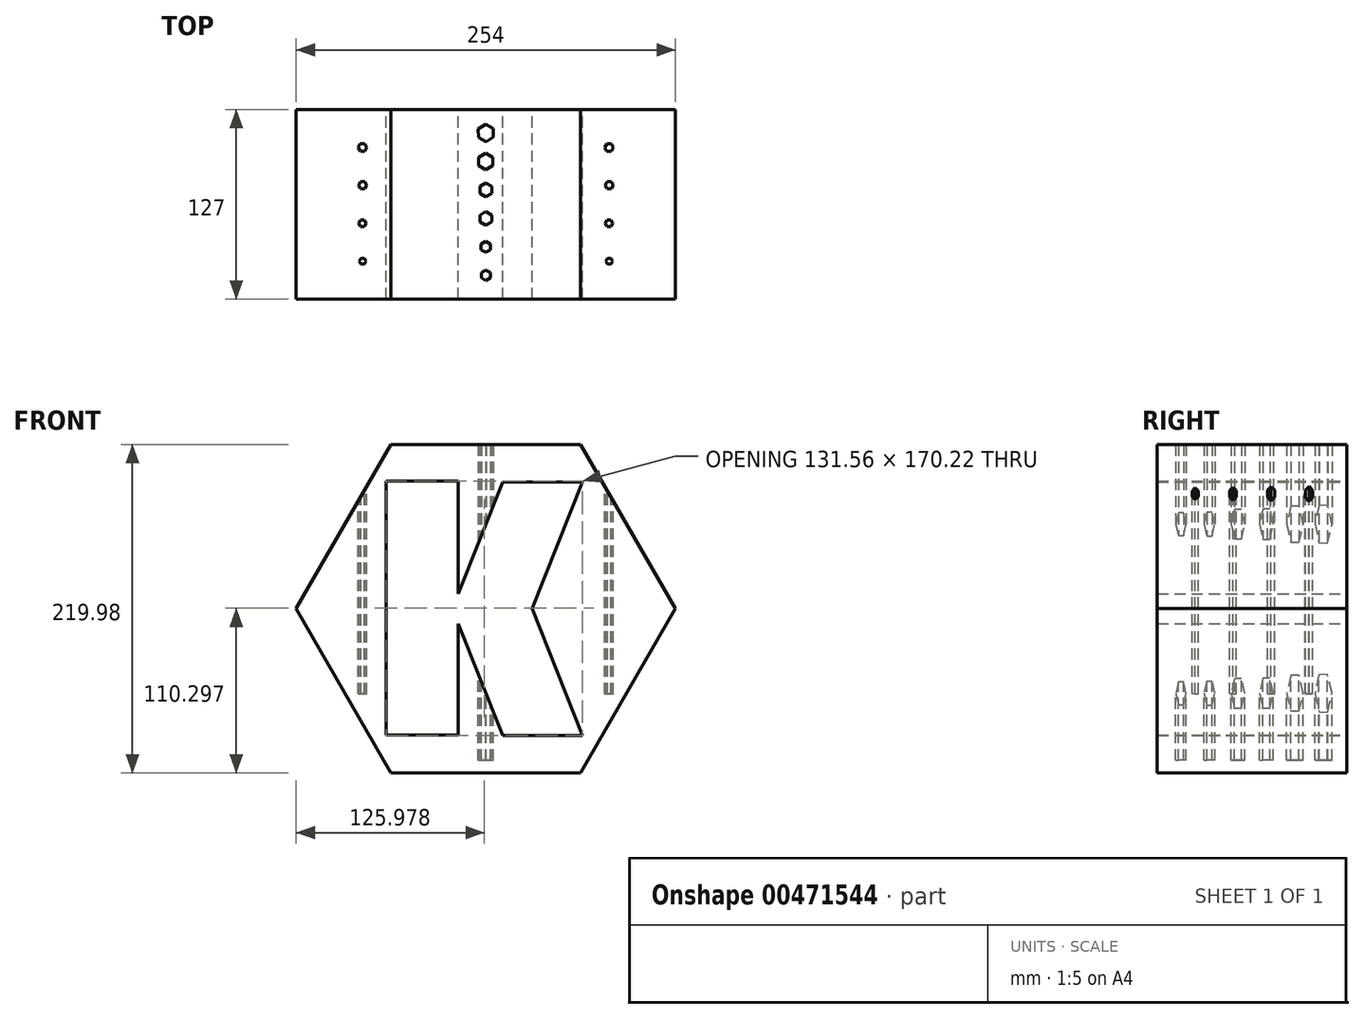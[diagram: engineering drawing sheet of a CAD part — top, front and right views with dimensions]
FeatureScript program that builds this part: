
annotation { "Feature Type Name" : "Feature", "Feature Type Description" : "" }
export const myFeature = defineFeature(function(context is Context, id is Id, definition is map)
    precondition{}
    {
        {
            var Q0;
            Q0=qCreatedBy(makeId("Front.planeOp"),FACE);
            var sketch = newSketch(context, id + "F0", { "sketchPlane" : qUnion([Q0])});
            skLineSegment(sketch, "E0.0", {"start": v(63.5, 109.99) * mm, "end": v(127, 0) * mm});
            skLineSegment(sketch, "E0.1", {"start": v(127, 0) * mm, "end": v(63.5, -109.99) * mm});
            skLineSegment(sketch, "E0.2", {"start": v(63.5, -109.99) * mm, "end": v(-63.5, -109.99) * mm});
            skLineSegment(sketch, "E0.3", {"start": v(-63.5, -109.99) * mm, "end": v(-127, 0) * mm});
            skLineSegment(sketch, "E0.4", {"start": v(-127, 0) * mm, "end": v(-63.5, 109.99) * mm});
            skLineSegment(sketch, "E0.5", {"start": v(-63.5, 109.99) * mm, "end": v(63.5, 109.99) * mm});
            skLineSegment(sketch, "E1.bottom", {"start": v(-66.8, 85.42) * mm, "end": v(-18.63, 85.42) * mm});
            skLineSegment(sketch, "E1.top", {"start": v(-66.8, -84.55) * mm, "end": v(-18.63, -84.55) * mm});
            skLineSegment(sketch, "E1.left", {"start": v(-66.8, 85.42) * mm, "end": v(-66.8, -84.55) * mm});
            skLineSegment(sketch, "E1.right", {"start": v(-18.63, 85.42) * mm, "end": v(-18.63, 9.98) * mm});
            skLineSegment(sketch, "E2.bottom", {"start": v(11.24, 84.8) * mm, "end": v(64.76, 84.8) * mm});
            skLineSegment(sketch, "E3.MirrorCS", {"start": v(11.24, -84.8) * mm, "end": v(64.76, -84.8) * mm});
            skLineSegment(sketch, "E4", {"start": v(11.24, 84.8) * mm, "end": v(-18.63, 9.98) * mm});
            skLineSegment(sketch, "E5.MirrorCS", {"start": v(11.24, -84.8) * mm, "end": v(-18.63, -9.98) * mm});
            skLineSegment(sketch, "E6", {"start": v(64.76, 84.8) * mm, "end": v(30.9, 0) * mm});
            skLineSegment(sketch, "E7.MirrorCS", {"start": v(64.76, -84.8) * mm, "end": v(30.9, 0) * mm});
            skLineSegment(sketch, "E8.trimOffspring", {"start": v(-18.63, -9.98) * mm, "end": v(-18.63, -84.55) * mm});
            skSolve(sketch);
        }
        {
            var Q0;
            Q0 = qSketchRegion(id + "F0", true);
            extrude(context, id + "F1", {"entities" : qUnion([Q0]), "endBound" : BoundingType.SYMMETRIC, "depth" : 127 * mm});
        }
        {
            var Q0;
            Q0=qCreatedBy(makeId("Top.planeOp"),FACE);
            var sketch = newSketch(context, id + "F2", { "sketchPlane" : qUnion([Q0])});
            skCircle(sketch, "E9.cCircle", {"center": v(-82.55, 38.1) * mm, "radius": 2.5 * mm, "construction": true});
            skLineSegment(sketch, "E9.0", {"start": v(-83.9, 35.55) * mm, "end": v(-85.44, 38) * mm});
            skLineSegment(sketch, "E9.1", {"start": v(-85.44, 38) * mm, "end": v(-84.08, 40.55) * mm});
            skLineSegment(sketch, "E9.2", {"start": v(-84.08, 40.55) * mm, "end": v(-81.2, 40.65) * mm});
            skLineSegment(sketch, "E9.3", {"start": v(-81.2, 40.65) * mm, "end": v(-79.66, 38.2) * mm});
            skLineSegment(sketch, "E9.4", {"start": v(-79.66, 38.2) * mm, "end": v(-81.02, 35.65) * mm});
            skLineSegment(sketch, "E9.5", {"start": v(-81.02, 35.65) * mm, "end": v(-83.9, 35.55) * mm});
            skPoint(sketch, "E9.0.midPoint", {"position": v(-84.67, 36.77) * mm});
            skCircle(sketch, "E10.cCircle", {"center": v(-82.55, 12.7) * mm, "radius": 2.38 * mm, "construction": true});
            skLineSegment(sketch, "E10.0", {"start": v(-83.92, 15.08) * mm, "end": v(-81.18, 15.08) * mm});
            skLineSegment(sketch, "E10.1", {"start": v(-81.18, 15.08) * mm, "end": v(-79.8, 12.7) * mm});
            skLineSegment(sketch, "E10.2", {"start": v(-79.8, 12.7) * mm, "end": v(-81.18, 10.32) * mm});
            skLineSegment(sketch, "E10.3", {"start": v(-81.18, 10.32) * mm, "end": v(-83.92, 10.32) * mm});
            skLineSegment(sketch, "E10.4", {"start": v(-83.92, 10.32) * mm, "end": v(-85.3, 12.7) * mm});
            skLineSegment(sketch, "E10.5", {"start": v(-85.3, 12.7) * mm, "end": v(-83.92, 15.08) * mm});
            skPoint(sketch, "E10.0.midPoint", {"position": v(-82.55, 15.08) * mm});
            skCircle(sketch, "E11.cCircle", {"center": v(-82.55, -12.7) * mm, "radius": 2.25 * mm, "construction": true});
            skLineSegment(sketch, "E11.0", {"start": v(-83.85, -10.45) * mm, "end": v(-81.25, -10.45) * mm});
            skLineSegment(sketch, "E11.1", {"start": v(-81.25, -10.45) * mm, "end": v(-79.95, -12.7) * mm});
            skLineSegment(sketch, "E11.2", {"start": v(-79.95, -12.7) * mm, "end": v(-81.25, -14.95) * mm});
            skLineSegment(sketch, "E11.3", {"start": v(-81.25, -14.95) * mm, "end": v(-83.85, -14.95) * mm});
            skLineSegment(sketch, "E11.4", {"start": v(-83.85, -14.95) * mm, "end": v(-85.15, -12.7) * mm});
            skLineSegment(sketch, "E11.5", {"start": v(-85.15, -12.7) * mm, "end": v(-83.85, -10.45) * mm});
            skPoint(sketch, "E11.0.midPoint", {"position": v(-82.55, -10.45) * mm});
            skCircle(sketch, "E12.cCircle", {"center": v(-82.55, -38.1) * mm, "radius": 1.98 * mm, "construction": true});
            skLineSegment(sketch, "E12.0", {"start": v(-83.7, -36.12) * mm, "end": v(-81.4, -36.12) * mm});
            skLineSegment(sketch, "E12.1", {"start": v(-81.4, -36.12) * mm, "end": v(-80.26, -38.1) * mm});
            skLineSegment(sketch, "E12.2", {"start": v(-80.26, -38.1) * mm, "end": v(-81.4, -40.08) * mm});
            skLineSegment(sketch, "E12.3", {"start": v(-81.4, -40.08) * mm, "end": v(-83.7, -40.08) * mm});
            skLineSegment(sketch, "E12.4", {"start": v(-83.7, -40.08) * mm, "end": v(-84.84, -38.1) * mm});
            skLineSegment(sketch, "E12.5", {"start": v(-84.84, -38.1) * mm, "end": v(-83.7, -36.12) * mm});
            skPoint(sketch, "E12.0.midPoint", {"position": v(-82.55, -36.12) * mm});
            skCircle(sketch, "E13.MirrorC", {"center": v(82.55, -38.1) * mm, "radius": 1.98 * mm, "construction": true});
            skLineSegment(sketch, "E14.MirrorCS", {"start": v(79.95, -12.7) * mm, "end": v(81.25, -14.95) * mm});
            skLineSegment(sketch, "E15.MirrorCS", {"start": v(83.7, -40.08) * mm, "end": v(84.84, -38.1) * mm});
            skLineSegment(sketch, "E16.MirrorCS", {"start": v(83.85, -14.95) * mm, "end": v(85.15, -12.7) * mm});
            skLineSegment(sketch, "E17.MirrorCS", {"start": v(84.84, -38.1) * mm, "end": v(83.7, -36.12) * mm});
            skLineSegment(sketch, "E18.MirrorCS", {"start": v(81.4, -40.08) * mm, "end": v(83.7, -40.08) * mm});
            skLineSegment(sketch, "E19.MirrorCS", {"start": v(81.4, -36.12) * mm, "end": v(80.26, -38.1) * mm});
            skLineSegment(sketch, "E20.MirrorCS", {"start": v(80.26, -38.1) * mm, "end": v(81.4, -40.08) * mm});
            skLineSegment(sketch, "E21.MirrorCS", {"start": v(81.25, -10.45) * mm, "end": v(79.95, -12.7) * mm});
            skLineSegment(sketch, "E22.MirrorCS", {"start": v(85.15, -12.7) * mm, "end": v(83.85, -10.45) * mm});
            skLineSegment(sketch, "E23.MirrorCS", {"start": v(83.7, -36.12) * mm, "end": v(81.4, -36.12) * mm});
            skLineSegment(sketch, "E24.MirrorCS", {"start": v(85.3, 12.7) * mm, "end": v(83.92, 15.08) * mm});
            skLineSegment(sketch, "E25.MirrorCS", {"start": v(81.18, 15.08) * mm, "end": v(79.8, 12.7) * mm});
            skLineSegment(sketch, "E26.MirrorCS", {"start": v(79.8, 12.7) * mm, "end": v(81.18, 10.32) * mm});
            skLineSegment(sketch, "E27.MirrorCS", {"start": v(81.18, 10.32) * mm, "end": v(83.92, 10.32) * mm});
            skLineSegment(sketch, "E28.MirrorCS", {"start": v(83.92, 10.32) * mm, "end": v(85.3, 12.7) * mm});
            skLineSegment(sketch, "E29.MirrorCS", {"start": v(81.02, 35.65) * mm, "end": v(83.9, 35.55) * mm});
            skLineSegment(sketch, "E30.MirrorCS", {"start": v(81.25, -14.95) * mm, "end": v(83.85, -14.95) * mm});
            skLineSegment(sketch, "E31.MirrorCS", {"start": v(79.66, 38.2) * mm, "end": v(81.02, 35.65) * mm});
            skLineSegment(sketch, "E32.MirrorCS", {"start": v(81.2, 40.65) * mm, "end": v(79.66, 38.2) * mm});
            skLineSegment(sketch, "E33.MirrorCS", {"start": v(83.92, 15.08) * mm, "end": v(81.18, 15.08) * mm});
            skLineSegment(sketch, "E34.MirrorCS", {"start": v(84.08, 40.55) * mm, "end": v(81.2, 40.65) * mm});
            skLineSegment(sketch, "E35.MirrorCS", {"start": v(85.44, 38) * mm, "end": v(84.08, 40.55) * mm});
            skLineSegment(sketch, "E36.MirrorCS", {"start": v(83.9, 35.55) * mm, "end": v(85.44, 38) * mm});
            skLineSegment(sketch, "E37.MirrorCS", {"start": v(83.85, -10.45) * mm, "end": v(81.25, -10.45) * mm});
            skPoint(sketch, "E38.MirrorP", {"position": v(84.67, 36.77) * mm});
            skPoint(sketch, "E39.MirrorP", {"position": v(82.55, 15.08) * mm});
            skPoint(sketch, "E40.MirrorP", {"position": v(82.55, -10.45) * mm});
            skPoint(sketch, "E41.MirrorP", {"position": v(82.55, -36.12) * mm});
            skCircle(sketch, "E42.MirrorC", {"center": v(82.55, -12.7) * mm, "radius": 2.25 * mm, "construction": true});
            skCircle(sketch, "E43.MirrorC", {"center": v(82.55, 12.7) * mm, "radius": 2.38 * mm, "construction": true});
            skCircle(sketch, "E44.MirrorC", {"center": v(82.55, 38.1) * mm, "radius": 2.5 * mm, "construction": true});
            skCircle(sketch, "E45.cCircle", {"center": v(0, 47.75) * mm, "radius": 5 * mm, "construction": true});
            skLineSegment(sketch, "E45.0", {"start": v(5.06, 44.98) * mm, "end": v(0.13, 41.98) * mm});
            skLineSegment(sketch, "E45.1", {"start": v(0.13, 41.98) * mm, "end": v(-4.93, 44.75) * mm});
            skLineSegment(sketch, "E45.2", {"start": v(-4.93, 44.75) * mm, "end": v(-5.06, 50.53) * mm});
            skLineSegment(sketch, "E45.3", {"start": v(-5.06, 50.53) * mm, "end": v(-0.13, 53.52) * mm});
            skLineSegment(sketch, "E45.4", {"start": v(-0.13, 53.52) * mm, "end": v(4.93, 50.75) * mm});
            skLineSegment(sketch, "E45.5", {"start": v(4.93, 50.75) * mm, "end": v(5.06, 44.98) * mm});
            skPoint(sketch, "E45.0.midPoint", {"position": v(2.6, 43.48) * mm});
            skCircle(sketch, "E46.cCircle", {"center": v(0, 28.68) * mm, "radius": 4.76 * mm, "construction": true});
            skLineSegment(sketch, "E46.0", {"start": v(4.76, 25.93) * mm, "end": v(0, 23.18) * mm});
            skLineSegment(sketch, "E46.1", {"start": v(0, 23.18) * mm, "end": v(-4.76, 25.94) * mm});
            skLineSegment(sketch, "E46.2", {"start": v(-4.76, 25.94) * mm, "end": v(-4.76, 31.43) * mm});
            skLineSegment(sketch, "E46.3", {"start": v(-4.76, 31.43) * mm, "end": v(0, 34.18) * mm});
            skLineSegment(sketch, "E46.4", {"start": v(0, 34.18) * mm, "end": v(4.76, 31.43) * mm});
            skLineSegment(sketch, "E46.5", {"start": v(4.76, 31.43) * mm, "end": v(4.76, 25.93) * mm});
            skPoint(sketch, "E46.0.midPoint", {"position": v(2.38, 24.56) * mm});
            skCircle(sketch, "E47.cCircle", {"center": v(0, 9.6) * mm, "radius": 4 * mm, "construction": true});
            skLineSegment(sketch, "E47.0", {"start": v(4, 11.92) * mm, "end": v(4, 7.3) * mm});
            skLineSegment(sketch, "E47.1", {"start": v(4, 7.3) * mm, "end": v(0, 5) * mm});
            skLineSegment(sketch, "E47.2", {"start": v(0, 5) * mm, "end": v(-4, 7.3) * mm});
            skLineSegment(sketch, "E47.3", {"start": v(-4, 7.3) * mm, "end": v(-4, 11.92) * mm});
            skLineSegment(sketch, "E47.4", {"start": v(-4, 11.92) * mm, "end": v(0, 14.23) * mm});
            skLineSegment(sketch, "E47.5", {"start": v(0, 14.23) * mm, "end": v(4, 11.92) * mm});
            skPoint(sketch, "E47.0.midPoint", {"position": v(4, 9.6) * mm});
            skCircle(sketch, "E48.cCircle", {"center": v(0, -9.47) * mm, "radius": 3.97 * mm, "construction": true});
            skLineSegment(sketch, "E48.0", {"start": v(3.97, -11.76) * mm, "end": v(0, -14.05) * mm});
            skLineSegment(sketch, "E48.1", {"start": v(0, -14.05) * mm, "end": v(-3.97, -11.76) * mm});
            skLineSegment(sketch, "E48.2", {"start": v(-3.97, -11.76) * mm, "end": v(-3.97, -7.17) * mm});
            skLineSegment(sketch, "E48.3", {"start": v(-3.97, -7.17) * mm, "end": v(0, -4.88) * mm});
            skLineSegment(sketch, "E48.4", {"start": v(0, -4.88) * mm, "end": v(3.97, -7.18) * mm});
            skLineSegment(sketch, "E48.5", {"start": v(3.97, -7.18) * mm, "end": v(3.97, -11.76) * mm});
            skPoint(sketch, "E48.0.midPoint", {"position": v(1.98, -12.9) * mm});
            skCircle(sketch, "E49.cCircle", {"center": v(0, -28.54) * mm, "radius": 3.17 * mm, "construction": true});
            skLineSegment(sketch, "E49.0", {"start": v(3.17, -26.7) * mm, "end": v(3.17, -30.38) * mm});
            skLineSegment(sketch, "E49.1", {"start": v(3.17, -30.38) * mm, "end": v(0, -32.2) * mm});
            skLineSegment(sketch, "E49.2", {"start": v(0, -32.2) * mm, "end": v(-3.18, -30.38) * mm});
            skLineSegment(sketch, "E49.3", {"start": v(-3.18, -30.38) * mm, "end": v(-3.18, -26.7) * mm});
            skLineSegment(sketch, "E49.4", {"start": v(-3.18, -26.7) * mm, "end": v(0, -24.88) * mm});
            skLineSegment(sketch, "E49.5", {"start": v(0, -24.88) * mm, "end": v(3.17, -26.7) * mm});
            skPoint(sketch, "E49.0.midPoint", {"position": v(3.17, -28.54) * mm});
            skCircle(sketch, "E50.cCircle", {"center": v(0, -47.62) * mm, "radius": 3 * mm, "construction": true});
            skLineSegment(sketch, "E50.0", {"start": v(3, -45.89) * mm, "end": v(3, -49.35) * mm});
            skLineSegment(sketch, "E50.1", {"start": v(3, -49.35) * mm, "end": v(0, -51.08) * mm});
            skLineSegment(sketch, "E50.2", {"start": v(0, -51.08) * mm, "end": v(-3, -49.35) * mm});
            skLineSegment(sketch, "E50.3", {"start": v(-3, -49.35) * mm, "end": v(-3, -45.89) * mm});
            skLineSegment(sketch, "E50.4", {"start": v(-3, -45.89) * mm, "end": v(0, -44.15) * mm});
            skLineSegment(sketch, "E50.5", {"start": v(0, -44.15) * mm, "end": v(3, -45.89) * mm});
            skPoint(sketch, "E50.0.midPoint", {"position": v(3, -47.62) * mm});
            skSolve(sketch);
        }
        {
            var Q0;
            Q0=makeQuery(id+"F2.imprint","IMPRINT",FACE,{"disambiguationData":[TD([[makeQuery(id+"F2.imprint","IMPRINT",EDGE,{"derivedFrom":sQuery(id+"F2.wireOp",EDGE,"E10.0")}),-1.0]])]});
            var Q1;
            Q1=makeQuery(id+"F2.imprint","IMPRINT",FACE,{"disambiguationData":[TD([[makeQuery(id+"F2.imprint","IMPRINT",EDGE,{"derivedFrom":sQuery(id+"F2.wireOp",EDGE,"E11.0")}),-1.0]])]});
            var Q2;
            Q2=makeQuery(id+"F2.imprint","IMPRINT",FACE,{"disambiguationData":[TD([[makeQuery(id+"F2.imprint","IMPRINT",EDGE,{"derivedFrom":sQuery(id+"F2.wireOp",EDGE,"E12.0")}),-1.0]])]});
            var Q3;
            Q3=makeQuery(id+"F2.imprint","IMPRINT",FACE,{"disambiguationData":[TD([[makeQuery(id+"F2.imprint","IMPRINT",EDGE,{"derivedFrom":sQuery(id+"F2.wireOp",EDGE,"E9.0")}),-1.0]])]});
            var Q4;
            Q4=makeQuery(id+"F2.imprint","IMPRINT",FACE,{"disambiguationData":[TD([[makeQuery(id+"F2.imprint","IMPRINT",EDGE,{"derivedFrom":sQuery(id+"F2.wireOp",EDGE,"E29.MirrorCS")}),1.0]])]});
            var Q5;
            Q5=makeQuery(id+"F2.imprint","IMPRINT",FACE,{"disambiguationData":[TD([[makeQuery(id+"F2.imprint","IMPRINT",EDGE,{"derivedFrom":sQuery(id+"F2.wireOp",EDGE,"E24.MirrorCS")}),1.0]])]});
            var Q6;
            Q6=makeQuery(id+"F2.imprint","IMPRINT",FACE,{"disambiguationData":[TD([[makeQuery(id+"F2.imprint","IMPRINT",EDGE,{"derivedFrom":sQuery(id+"F2.wireOp",EDGE,"E14.MirrorCS")}),1.0]])]});
            var Q7;
            Q7=makeQuery(id+"F2.imprint","IMPRINT",FACE,{"disambiguationData":[TD([[makeQuery(id+"F2.imprint","IMPRINT",EDGE,{"derivedFrom":sQuery(id+"F2.wireOp",EDGE,"E15.MirrorCS")}),1.0]])]});
            extrude(context, id + "F3", {"entities" : qUnion([Q0, Q1, Q2, Q3, Q4, Q5, Q6, Q7]), "operationType" : NewBodyOperationType.REMOVE, "oppositeDirection" : true, "depth" : 57.15 * mm});
        }
        {
            var Q0;
            Q0 = qSketchRegion(id + "F2", true);
            extrude(context, id + "F4", {"entities" : qUnion([Q0]), "operationType" : NewBodyOperationType.REMOVE, "depth" : 127 * mm});
        }
        {
            var Q0;
            Q0=makeQuery(id+"F2.imprint","IMPRINT",FACE,{"disambiguationData":[TD([[makeQuery(id+"F2.imprint","IMPRINT",EDGE,{"derivedFrom":sQuery(id+"F2.wireOp",EDGE,"E48.0")}),-1.0]])]});
            var Q1;
            Q1=makeQuery(id+"F2.imprint","IMPRINT",FACE,{"disambiguationData":[TD([[makeQuery(id+"F2.imprint","IMPRINT",EDGE,{"derivedFrom":sQuery(id+"F2.wireOp",EDGE,"E49.0")}),-1.0]])]});
            var Q2;
            Q2=makeQuery(id+"F2.imprint","IMPRINT",FACE,{"disambiguationData":[TD([[makeQuery(id+"F2.imprint","IMPRINT",EDGE,{"derivedFrom":sQuery(id+"F2.wireOp",EDGE,"E47.0")}),-1.0]])]});
            var Q3;
            Q3=makeQuery(id+"F2.imprint","IMPRINT",FACE,{"disambiguationData":[TD([[makeQuery(id+"F2.imprint","IMPRINT",EDGE,{"derivedFrom":sQuery(id+"F2.wireOp",EDGE,"E46.0")}),-1.0]])]});
            var Q4;
            Q4=makeQuery(id+"F2.imprint","IMPRINT",FACE,{"disambiguationData":[TD([[makeQuery(id+"F2.imprint","IMPRINT",EDGE,{"derivedFrom":sQuery(id+"F2.wireOp",EDGE,"E50.0")}),-1.0]])]});
            var Q5;
            Q5=makeQuery(id+"F2.imprint","IMPRINT",FACE,{"disambiguationData":[TD([[makeQuery(id+"F2.imprint","IMPRINT",EDGE,{"derivedFrom":sQuery(id+"F2.wireOp",EDGE,"E45.0")}),-1.0]])]});
            extrude(context, id + "F5", {"entities" : qUnion([Q0, Q1, Q2, Q3, Q4, Q5]), "operationType" : NewBodyOperationType.REMOVE, "oppositeDirection" : true, "depth" : 101.6 * mm});
        }
    });
